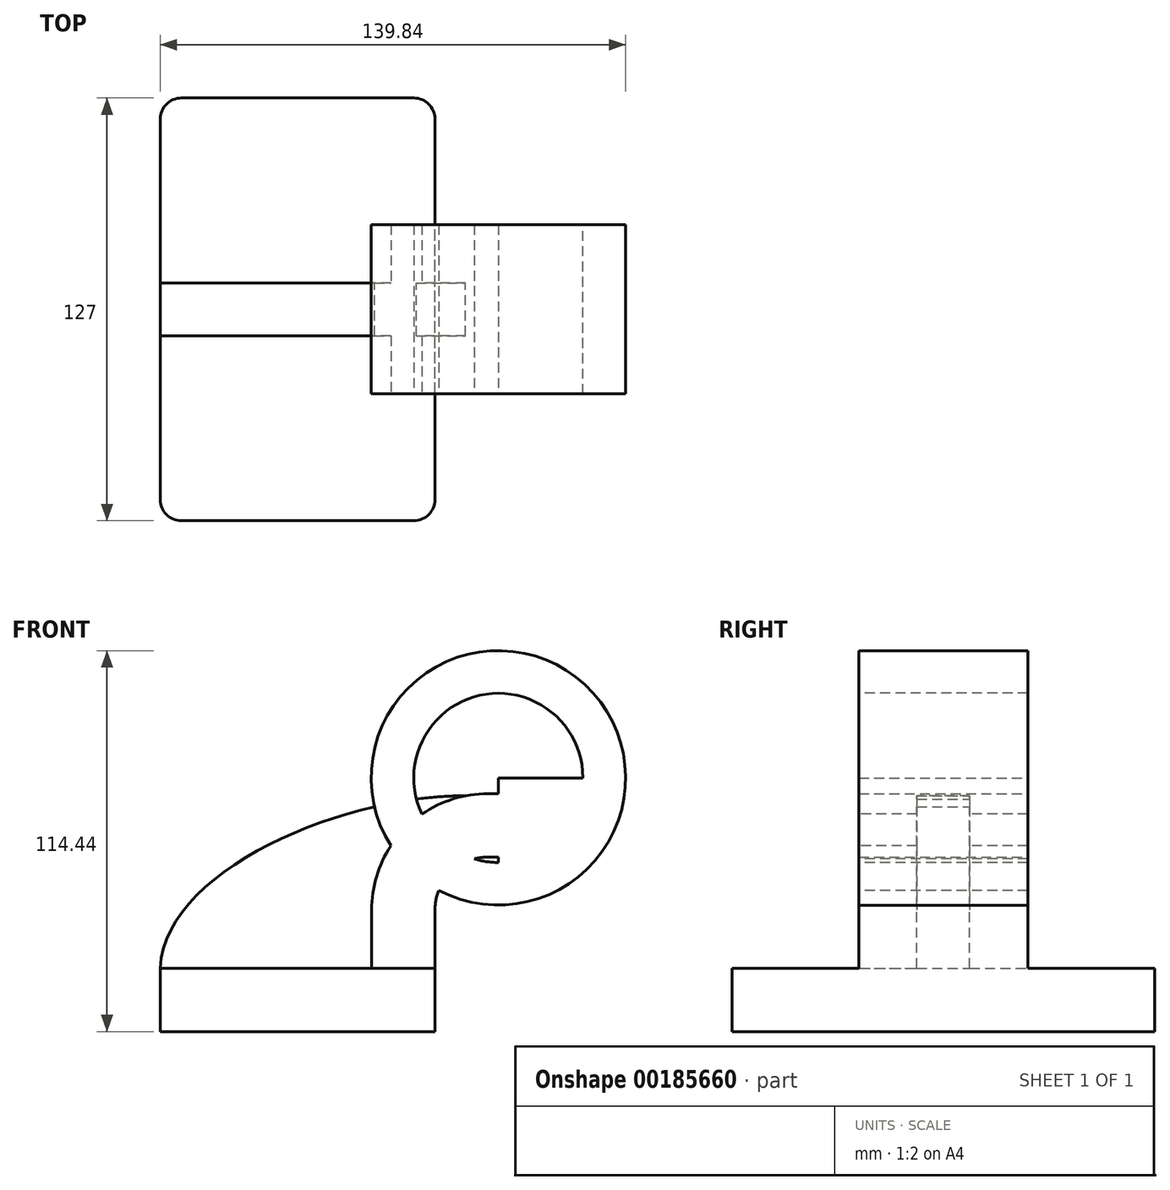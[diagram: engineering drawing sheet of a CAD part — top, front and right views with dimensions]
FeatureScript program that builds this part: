
annotation { "Feature Type Name" : "Feature", "Feature Type Description" : "" }
export const myFeature = defineFeature(function(context is Context, id is Id, definition is map)
    precondition{}
    {
        {
            var Q0;
            Q0=qCreatedBy(makeId("Front.planeOp"),FACE);
            var sketch = newSketch(context, id + "F0", { "sketchPlane" : qUnion([Q0])});
            skLineSegment(sketch, "E0.bottom", {"start": v(-41.28, -9.53) * mm, "end": v(41.28, -9.53) * mm});
            skLineSegment(sketch, "E0.top", {"start": v(-41.28, 9.52) * mm, "end": v(41.28, 9.52) * mm});
            skLineSegment(sketch, "E0.left", {"start": v(-41.28, -9.53) * mm, "end": v(-41.28, 9.52) * mm});
            skLineSegment(sketch, "E0.right", {"start": v(41.28, -9.53) * mm, "end": v(41.28, 9.52) * mm});
            skPoint(sketch, "E0.middle", {"position": v(0, 0) * mm});
            skLineSegment(sketch, "E1.bottom", {"start": v(60.33, 38.1) * mm, "end": v(111.12, 38.1) * mm});
            skLineSegment(sketch, "E1.top", {"start": v(60.33, 66.67) * mm, "end": v(111.12, 66.67) * mm});
            skLineSegment(sketch, "E1.left", {"start": v(60.33, 38.1) * mm, "end": v(60.33, 66.67) * mm});
            skLineSegment(sketch, "E1.right", {"start": v(111.12, 38.1) * mm, "end": v(111.12, 66.67) * mm});
            skPoint(sketch, "E1.middle", {"position": v(85.72, 52.39) * mm});
            skLineSegment(sketch, "E2", {"start": v(41.27, 9.52) * mm, "end": v(41.27, 27) * mm});
            skArc(sketch, "E3", {"start": v(41.27, 27) * mm, "mid": v(45.92, 38.23) * mm, "end": v(57.15, 42.88) * mm});
            skLineSegment(sketch, "E4", {"start": v(57.15, 42.88) * mm, "end": v(85.74, 42.88) * mm});
            skLineSegment(sketch, "E5.0", {"start": v(57.15, 61.93) * mm, "end": v(85.74, 61.93) * mm});
            skArc(sketch, "E5.1", {"start": v(22.23, 27) * mm, "mid": v(32.45, 51.7) * mm, "end": v(57.15, 61.93) * mm});
            skLineSegment(sketch, "E5.2", {"start": v(22.23, 9.52) * mm, "end": v(22.23, 27) * mm});
            skLineSegment(sketch, "E6", {"start": v(85.72, 38.1) * mm, "end": v(85.74, 66.67) * mm});
            skFitSpline(sketch, "E7", {"points": [v(-41.28, 9.53) * mm, v(50.47, 61.28) * mm], "startDerivative": vector(4.13, 88.57) * mm, "endDerivative": vector(110.68, -0.8) * mm});
            skSolve(sketch);
        }
        {
            var Q0;
            Q0=makeQuery(id+"F0.imprint","IMPRINT",FACE,{"disambiguationData":[TD([[makeQuery(id+"F0.imprint","IMPRINT",EDGE,{"derivedFrom":sQuery(id+"F0.wireOp",EDGE,"E0.bottom")}),1.0]])]});
            extrude(context, id + "F1", {"entities" : qUnion([Q0]), "endBound" : BoundingType.SYMMETRIC, "depth" : 127 * mm});
        }
        {
            var Q0;
            Q0=makeQuery(id+"F0.imprint","IMPRINT",FACE,{"disambiguationData":[TD([[makeQuery(id+"F0.imprint","IMPRINT",EDGE,{"derivedFrom":sQuery(id+"F0.wireOp",EDGE,"E0.bottom")}),1.0]])]});
            var Q1;
            {var subQ0=sQuery(id+"F0.wireOp",EDGE,"E1.left");var subQ1=sQuery(id+"F0.wireOp",EDGE,"E1.bottom");var subQ2=makeQuery(id+"F0.imprint","INTERSECT",VERTEX,{"derivedFrom":[subQ1,subQ0]});Q1=makeQuery(id+"F0.imprint","IMPRINT",FACE,{"disambiguationData":[TD([[makeQuery(id+"F0.imprint","IMPRINT",EDGE,{"disambiguationData":[TD([[subQ2,-1.0]])],"derivedFrom":subQ1}),1.0]])]});}
            var Q2;
            {var subQ0=sQuery(id+"F0.wireOp",EDGE,"E1.left");var subQ1=sQuery(id+"F0.wireOp",EDGE,"E1.top");var subQ2=makeQuery(id+"F0.imprint","INTERSECT",VERTEX,{"derivedFrom":[subQ1,subQ0]});Q2=makeQuery(id+"F0.imprint","IMPRINT",FACE,{"disambiguationData":[TD([[makeQuery(id+"F0.imprint","IMPRINT",EDGE,{"disambiguationData":[TD([[subQ2,-1.0]])],"derivedFrom":subQ1}),-1.0]])]});}
            var Q3;
            {var subQ0=sQuery(id+"F0.wireOp",EDGE,"E4");var subQ1=sQuery(id+"F0.wireOp",EDGE,"E1.left");var subQ2=makeQuery(id+"F0.imprint","INTERSECT",VERTEX,{"derivedFrom":[subQ1,subQ0]});Q3=makeQuery(id+"F0.imprint","IMPRINT",FACE,{"disambiguationData":[TD([[makeQuery(id+"F0.imprint","IMPRINT",EDGE,{"disambiguationData":[TD([[subQ2,-1.0]])],"derivedFrom":subQ1}),-1.0]])]});}
            var Q4;
            {var subQ1=sQuery(id+"F0.wireOp",EDGE,"E2");Q4=makeQuery(id+"F0.imprint","IMPRINT",FACE,{"disambiguationData":[TD([[makeQuery(id+"F0.imprint","IMPRINT",EDGE,{"derivedFrom":subQ1}),1.0]])]});}
            extrude(context, id + "F2", {"entities" : qUnion([Q0, Q1, Q2, Q3, Q4]), "operationType" : NewBodyOperationType.ADD, "endBound" : BoundingType.SYMMETRIC, "depth" : 50.8 * mm});
        }
        {
            var Q0;
            Q0=makeQuery(id+"F0.imprint","IMPRINT",FACE,{"disambiguationData":[TD([[makeQuery(id+"F0.imprint","IMPRINT",EDGE,{"derivedFrom":sQuery(id+"F0.wireOp",EDGE,"E0.bottom")}),1.0]])]});
            var Q1;
            {var subQ0=sQuery(id+"F0.wireOp",EDGE,"E1.left");var subQ1=sQuery(id+"F0.wireOp",EDGE,"E1.bottom");var subQ2=makeQuery(id+"F0.imprint","INTERSECT",VERTEX,{"derivedFrom":[subQ1,subQ0]});Q1=makeQuery(id+"F0.imprint","IMPRINT",FACE,{"disambiguationData":[TD([[makeQuery(id+"F0.imprint","IMPRINT",EDGE,{"disambiguationData":[TD([[subQ2,-1.0]])],"derivedFrom":subQ1}),1.0]])]});}
            var Q2;
            {var subQ0=sQuery(id+"F0.wireOp",EDGE,"E1.left");var subQ1=sQuery(id+"F0.wireOp",EDGE,"E1.top");var subQ2=makeQuery(id+"F0.imprint","INTERSECT",VERTEX,{"derivedFrom":[subQ1,subQ0]});Q2=makeQuery(id+"F0.imprint","IMPRINT",FACE,{"disambiguationData":[TD([[makeQuery(id+"F0.imprint","IMPRINT",EDGE,{"disambiguationData":[TD([[subQ2,-1.0]])],"derivedFrom":subQ1}),-1.0]])]});}
            var Q3;
            {var subQ1=sQuery(id+"F0.wireOp",EDGE,"E2");Q3=makeQuery(id+"F0.imprint","IMPRINT",FACE,{"disambiguationData":[TD([[makeQuery(id+"F0.imprint","IMPRINT",EDGE,{"derivedFrom":subQ1}),1.0]])]});}
            var Q4;
            {var subQ0=sQuery(id+"F0.wireOp",EDGE,"E4");var subQ1=sQuery(id+"F0.wireOp",EDGE,"E1.left");var subQ2=makeQuery(id+"F0.imprint","INTERSECT",VERTEX,{"derivedFrom":[subQ1,subQ0]});Q4=makeQuery(id+"F0.imprint","IMPRINT",FACE,{"disambiguationData":[TD([[makeQuery(id+"F0.imprint","IMPRINT",EDGE,{"disambiguationData":[TD([[subQ2,-1.0]])],"derivedFrom":subQ1}),-1.0]])]});}
            var Q5;
            {var subQ2=sQuery(id+"F0.wireOp",EDGE,"E5.2");Q5=makeQuery(id+"F0.imprint","IMPRINT",FACE,{"disambiguationData":[TD([[makeQuery(id+"F0.imprint","IMPRINT",EDGE,{"derivedFrom":subQ2}),1.0]])]});}
            extrude(context, id + "F3", {"entities" : qUnion([Q0, Q1, Q2, Q3, Q4, Q5]), "operationType" : NewBodyOperationType.ADD, "endBound" : BoundingType.SYMMETRIC, "depth" : 15.88 * mm});
        }
        {
            var Q0;
            Q0=makeQuery(id+"F2.opExtrude","SWEPT_FACE",FACE,{"disambiguationData":[OSD([sQuery(id+"F0.wireOp",EDGE,"E6")])]});
            var Q1;
            Q1=makeQuery(id+"F2.opExtrude","SWEPT_EDGE",EDGE,{"disambiguationData":[OSD([sQuery(id+"F0.wireOp",EDGE,"E1.top"),sQuery(id+"F0.wireOp",EDGE,"E1.left")])]});
            revolve(context, id + "F4", {"operationType" : NewBodyOperationType.ADD, "entities" : qUnion([Q0]), "axis" : qUnion([Q1]), "revolveType" : RevolveType.FULL});
        }
        {
            var Q0;
            Q0=makeQuery(id+"F1.opExtrude","CAP_EDGE",EDGE,{"disambiguationData":[OSD([sQuery(id+"F0.wireOp",EDGE,"E0.left")])],"isStart":false});
            var Q1;
            Q1=makeQuery(id+"F1.opExtrude","CAP_EDGE",EDGE,{"disambiguationData":[OSD([sQuery(id+"F0.wireOp",EDGE,"E0.left")])],"isStart":true});
            var Q2;
            Q2=makeQuery(id+"F1.opExtrude","CAP_EDGE",EDGE,{"disambiguationData":[OSD([sQuery(id+"F0.wireOp",EDGE,"E0.right")])],"isStart":false});
            var Q3;
            Q3=makeQuery(id+"F1.opExtrude","CAP_EDGE",EDGE,{"disambiguationData":[OSD([sQuery(id+"F0.wireOp",EDGE,"E0.right")])],"isStart":true});
            fillet(context, id + "F5", {"entities" : qUnion([Q0, Q1, Q2, Q3]), "radius" : 6.35 * mm, "tangentPropagation" : true, "allowEdgeOverflow" : false});
        }
    });
